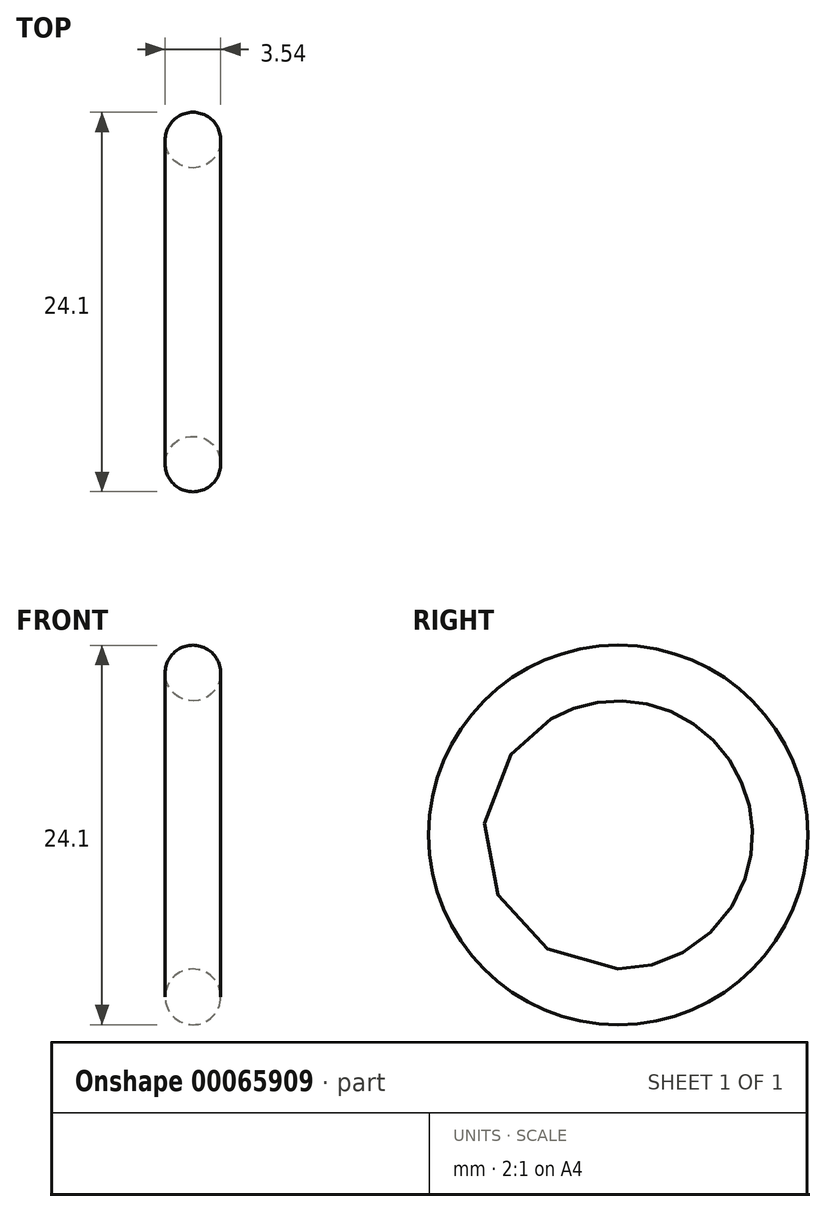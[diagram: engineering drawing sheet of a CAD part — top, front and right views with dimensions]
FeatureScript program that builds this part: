
annotation { "Feature Type Name" : "Feature", "Feature Type Description" : "" }
export const myFeature = defineFeature(function(context is Context, id is Id, definition is map)
    precondition{}
    {
        {
            var Q0;
            Q0=qCreatedBy(makeId("Front.planeOp"),FACE);
            var sketch = newSketch(context, id + "F0", { "sketchPlane" : qUnion([Q0])});
            skLineSegment(sketch, "E0", {"start": v(0, 0) * mm, "end": v(-6.06, 0) * mm, "construction": true});
            skCircle(sketch, "E1", {"center": v(0, 10.29) * mm, "radius": 1.77 * mm});
            skSolve(sketch);
        }
        {
            var Q0;
            Q0=makeQuery(id+"F0.imprint","IMPRINT",FACE,{"disambiguationData":[TD([[makeQuery(id+"F0.imprint","IMPRINT",EDGE,{"derivedFrom":sQuery(id+"F0.wireOp",EDGE,"E1")}),1.0]])]});
            var Q1;
            Q1=sQuery(id+"F0.wireOp",EDGE,"E0");
            revolve(context, id + "F1", {"entities" : qUnion([Q0]), "axis" : qUnion([Q1]), "revolveType" : RevolveType.FULL});
        }
    });
